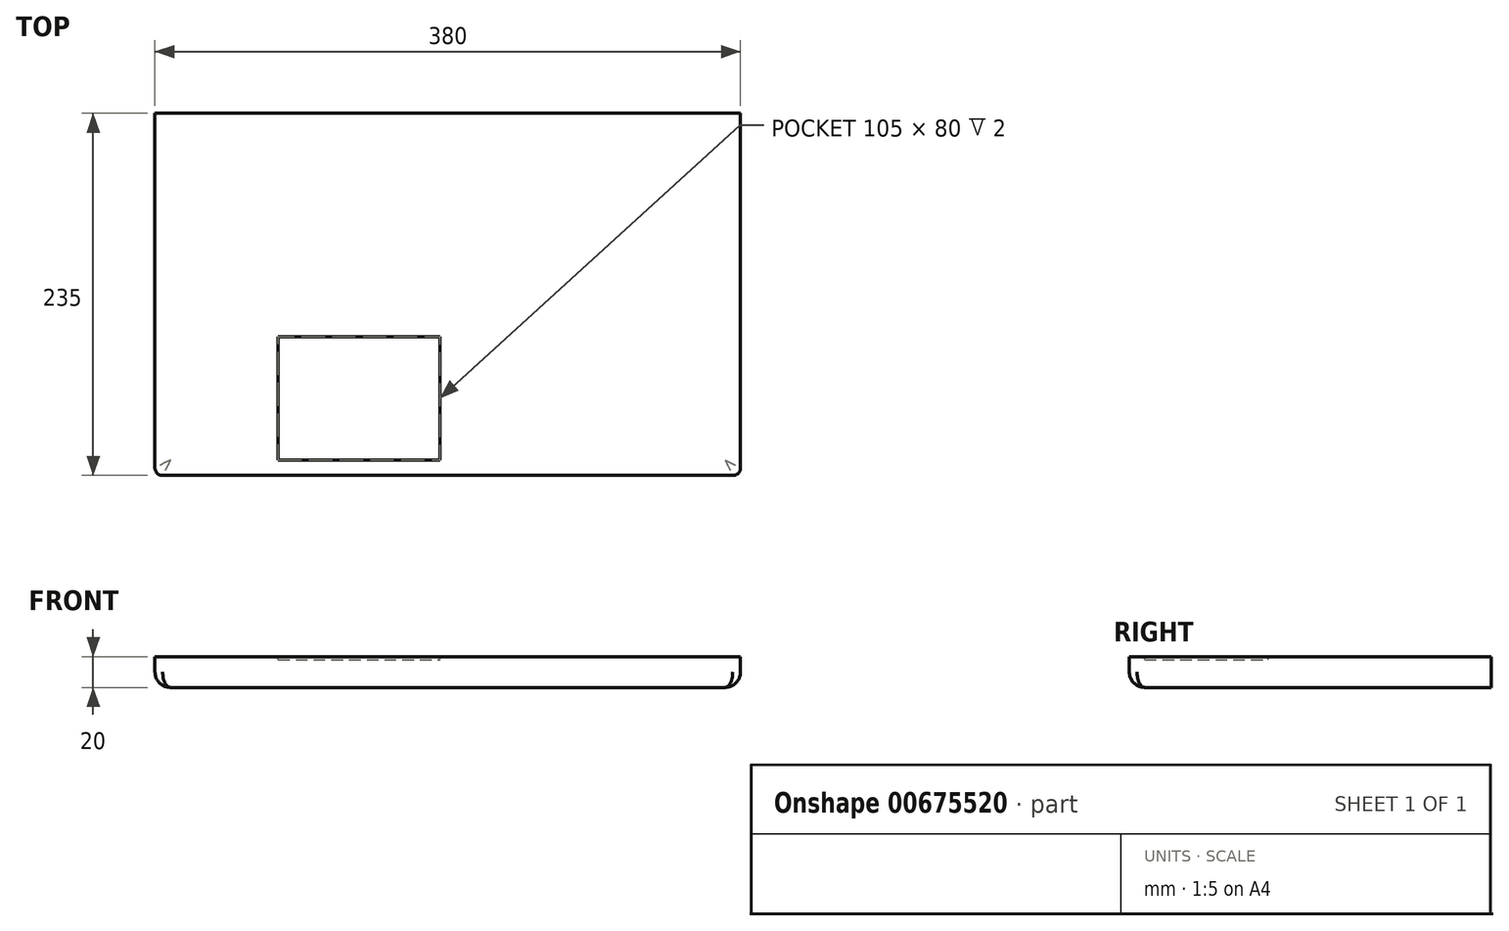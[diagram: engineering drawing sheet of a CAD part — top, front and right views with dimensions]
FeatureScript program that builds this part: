
annotation { "Feature Type Name" : "Feature", "Feature Type Description" : "" }
export const myFeature = defineFeature(function(context is Context, id is Id, definition is map)
    precondition{}
    {
        {
            var Q0;
            Q0=qCreatedBy(makeId("Top.planeOp"),FACE);
            var sketch = newSketch(context, id + "F0", { "sketchPlane" : qUnion([Q0])});
            skLineSegment(sketch, "E0", {"start": v(-190, 117.5) * mm, "end": v(190, 117.5) * mm});
            skLineSegment(sketch, "E1", {"start": v(-190, 117.5) * mm, "end": v(-190, -117.5) * mm});
            skLineSegment(sketch, "E2", {"start": v(-190, -117.5) * mm, "end": v(190, -117.5) * mm});
            skLineSegment(sketch, "E3", {"start": v(190, 117.5) * mm, "end": v(190, -117.5) * mm});
            skSolve(sketch);
        }
        {
            var Q0;
            Q0 = qSketchRegion(id + "F0", true);
            extrude(context, id + "F1", {"entities" : qUnion([Q0]), "depth" : 20 * mm, "offsetDistance" : 25 * mm});
        }
        {
            var Q0;
            Q0=makeQuery(id+"F1.opExtrude","CAP_FACE",FACE,{"disambiguationData":[OSD([sQuery(id+"F0.wireOp",EDGE,"E0"),sQuery(id+"F0.wireOp",EDGE,"E1"),sQuery(id+"F0.wireOp",EDGE,"E2"),sQuery(id+"F0.wireOp",EDGE,"E3")])],"isStart":false});
            var sketch = newSketch(context, id + "F2", { "sketchPlane" : qUnion([Q0])});
            skLineSegment(sketch, "E4.bottom", {"start": v(-110, -107.5) * mm, "end": v(-5, -107.5) * mm});
            skLineSegment(sketch, "E4.top", {"start": v(-110, -27.5) * mm, "end": v(-5, -27.5) * mm});
            skLineSegment(sketch, "E4.left", {"start": v(-110, -107.5) * mm, "end": v(-110, -27.5) * mm});
            skLineSegment(sketch, "E4.right", {"start": v(-5, -107.5) * mm, "end": v(-5, -27.5) * mm});
            skSolve(sketch);
        }
        {
            var Q0;
            Q0 = qSketchRegion(id + "F2", true);
            extrude(context, id + "F3", {"entities" : qUnion([Q0]), "operationType" : NewBodyOperationType.REMOVE, "oppositeDirection" : true, "depth" : 2 * mm, "offsetDistance" : 25 * mm});
        }
        {
            var Q0;
            Q0=makeQuery(id+"F1.opExtrude","SWEPT_EDGE",EDGE,{"disambiguationData":[OSD([sQuery(id+"F0.wireOp",EDGE,"E1"),sQuery(id+"F0.wireOp",EDGE,"E2")])]});
            var Q1;
            Q1=makeQuery(id+"F1.opExtrude","SWEPT_EDGE",EDGE,{"disambiguationData":[OSD([sQuery(id+"F0.wireOp",EDGE,"E2"),sQuery(id+"F0.wireOp",EDGE,"E3")])]});
            fillet(context, id + "F4", {"entities" : qUnion([Q0, Q1]), "radius" : 5 * mm, "tangentPropagation" : true, "allowEdgeOverflow" : false});
        }
        {
            var Q0;
            Q0=makeQuery(id+"F1.opExtrude","CAP_EDGE",EDGE,{"disambiguationData":[OSD([sQuery(id+"F0.wireOp",EDGE,"E2")])],"isStart":true});
            fillet(context, id + "F5", {"entities" : qUnion([Q0]), "radius" : 10 * mm, "tangentPropagation" : true, "allowEdgeOverflow" : false});
        }
    });
